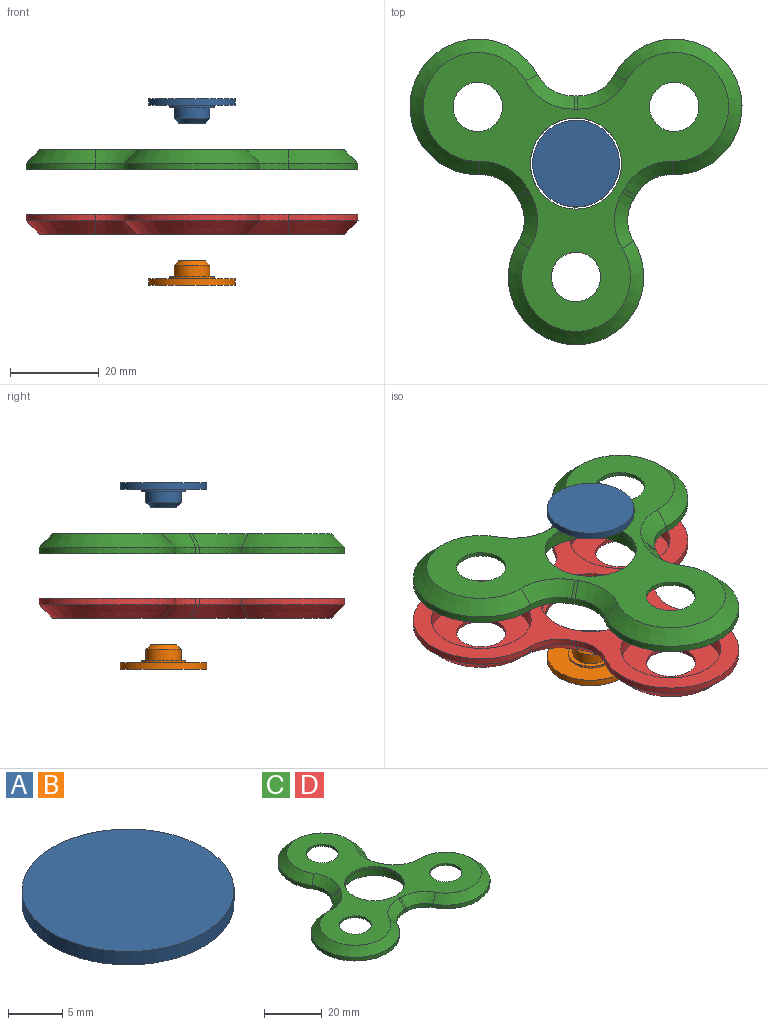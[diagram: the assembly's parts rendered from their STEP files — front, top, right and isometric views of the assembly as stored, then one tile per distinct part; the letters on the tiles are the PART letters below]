
ASSEMBLY  parts=4 mates=3
PART A: 10 faces, bbox 19.5x19.5x5.5 mm
  f0: cylinder r=2mm len=4mm, axis (0,0,1), area 50.3mm2, adj f2,f3
  f1: cylinder r=4mm len=8mm, axis (0,0,1), area 62.8mm2, adj f4,f6
  f2: plane 6x6mm, normal (0,0,-1), area 15.7mm2, adj f0,f4
  f3: plane 4x4mm, normal (0,0,-1), area 12.6mm2, adj f0
  f4: cone r=3mm half-angle=45deg, axis (0,0,1), area 31.1mm2, adj f1,f2
  f5: cylinder r=5mm len=10mm, axis (0,0,1), area 15.7mm2, adj f6,f9
  f6: plane 10x10mm, normal (0,0,-1), area 28.3mm2, adj f1,f5
  f7: plane 19.5x19.5mm, normal (0,0,1), area 298.6mm2, adj f8
  f8: cylinder r=9.75mm len=19.5mm, axis (0,0,1), area 91.9mm2, adj f7,f9
  f9: plane 19.5x19.5mm, normal (0,0,-1), area 220.1mm2, adj f5,f8
PART B: same geometry as A
PART C: 38 faces, bbox 74.7x68.8x4.5 mm
  f0: cylinder r=11.25mm len=22.5mm, axis (0,0,-1), area 254.5mm2, adj f5,f37
  f1: cylinder r=11.25mm len=22.5mm, axis (0,0,-1), area 254.5mm2, adj f5,f35
  f2: cylinder r=11.25mm len=22.5mm, axis (0,0,-1), area 254.5mm2, adj f5,f33
  f3: cylinder r=11.25mm len=22.5mm, axis (0,0,-1), area 254.5mm2, adj f5,f31
  f4: plane 68.67x62.75mm, normal (0,0,1), area 1449.2mm2, adj f18,f19,f20,f21,f22,f23,f24,f25
  f5: plane 74.67x68.75mm, normal (0,0,-1), area 1221.7mm2, adj f0,f1,f2,f3,f6,f7,f8,f9
  f6: cylinder r=9mm len=8.2mm, axis (0,0,-1), area 14.9mm2, adj f5,f7,f17,f20
  f7: cylinder r=15.25mm len=30.5mm, axis (0,0,-1), area 97.2mm2, adj f5,f6,f8,f18
  f8: cylinder r=9mm len=8.2mm, axis (0,0,-1), area 14.9mm2, adj f5,f7,f9,f19
  f9: cylinder r=15.25mm len=1.5mm, axis (0,0,-1), area 1.4mm2, adj f5,f8,f10,f21
  f10: cylinder r=9mm len=8.2mm, axis (0,0,-1), area 14.9mm2, adj f5,f9,f11,f23
  f11: cylinder r=15.25mm len=30.5mm, axis (0,0,-1), area 97.2mm2, adj f5,f10,f12,f25
  f12: cylinder r=9mm len=8.2mm, axis (0,0,-1), area 14.9mm2, adj f5,f11,f13,f27
  f13: cylinder r=15.25mm len=1.5mm, axis (0,0,-1), area 1.4mm2, adj f5,f12,f14,f29
  f14: cylinder r=9mm len=9.46mm, axis (0,0,-1), area 14.9mm2, adj f5,f13,f15,f28
  f15: cylinder r=15.25mm len=30.5mm, axis (0,0,-1), area 97.2mm2, adj f5,f14,f16,f26
  f16: cylinder r=9mm len=9.46mm, axis (0,0,-1), area 14.9mm2, adj f5,f15,f17,f24
  f17: cylinder r=15.25mm len=1.5mm, axis (0,0,-1), area 1.4mm2, adj f5,f6,f16,f22
  f18: cone r=12.25mm half-angle=45deg, axis (0,0,-1), area 247.9mm2, adj f4,f7,f19,f20
  f19: cone r=9mm half-angle=45deg, axis (0,0,1), area 49.3mm2, adj f4,f8,f18,f21
  f20: cone r=9mm half-angle=45deg, axis (0,0,1), area 49.3mm2, adj f4,f6,f18,f22
  f21: cone r=12.25mm half-angle=45deg, axis (0,0,-1), area 3.5mm2, adj f4,f9,f19,f23
  f22: cone r=12.25mm half-angle=45deg, axis (0,0,-1), area 3.5mm2, adj f4,f17,f20,f24
  f23: cone r=9mm half-angle=45deg, axis (0,0,1), area 49.3mm2, adj f4,f10,f21,f25
  f24: cone r=9mm half-angle=45deg, axis (0,0,1), area 49.3mm2, adj f4,f16,f22,f26
  f25: cone r=12.25mm half-angle=45deg, axis (0,0,-1), area 247.9mm2, adj f4,f11,f23,f27
  f26: cone r=12.25mm half-angle=45deg, axis (0,0,-1), area 247.9mm2, adj f4,f15,f24,f28
  f27: cone r=9mm half-angle=45deg, axis (0,0,1), area 49.3mm2, adj f4,f12,f25,f29
  f28: cone r=9mm half-angle=45deg, axis (0,0,1), area 49.3mm2, adj f4,f14,f26,f29
  f29: cone r=12.25mm half-angle=45deg, axis (0,0,-1), area 3.5mm2, adj f4,f13,f27,f28
  f30: cylinder r=5.55mm len=11.1mm, axis (0,0,1), area 31.4mm2, adj f4,f31
  f31: plane 22.5x22.5mm, normal (0,0,-1), area 300.8mm2, adj f3,f30
  f32: cylinder r=10.25mm len=20.5mm, axis (0,0,1), area 58mm2, adj f4,f33
  f33: plane 22.5x22.5mm, normal (0,0,-1), area 67.5mm2, adj f2,f32
  f34: cylinder r=5.55mm len=11.1mm, axis (0,0,1), area 31.4mm2, adj f4,f35
  f35: plane 22.5x22.5mm, normal (0,0,-1), area 300.8mm2, adj f1,f34
  f36: cylinder r=5.55mm len=11.1mm, axis (0,0,1), area 31.4mm2, adj f4,f37
  f37: plane 22.5x22.5mm, normal (0,0,-1), area 300.8mm2, adj f0,f36
PART D: same geometry as C
PLACE A t=(-5.53,15.15,24.78)mm
PLACE B rot(axis=(1,0,0),180deg) t=(-5.53,15.15,-8.22)mm
PLACE C rot(axis=(0,0,-1),180deg) t=(-5.53,15.15,13.28)mm
PLACE D rot(axis=(1,0,0),180deg) t=(-5.53,15.15,3.28)mm
MATE slider B.f8 <-> D.f32  axis (0,0,1) through (-5.53,15.15,-11.22)mm
MATE cylindrical C.f2 <-> D.f2  axis (0,0,-1) through (-5.53,15.15,13.28)mm
MATE slider A.f8 <-> C.f32  axis (0,0,-1) through (-5.53,15.15,27.78)mm
